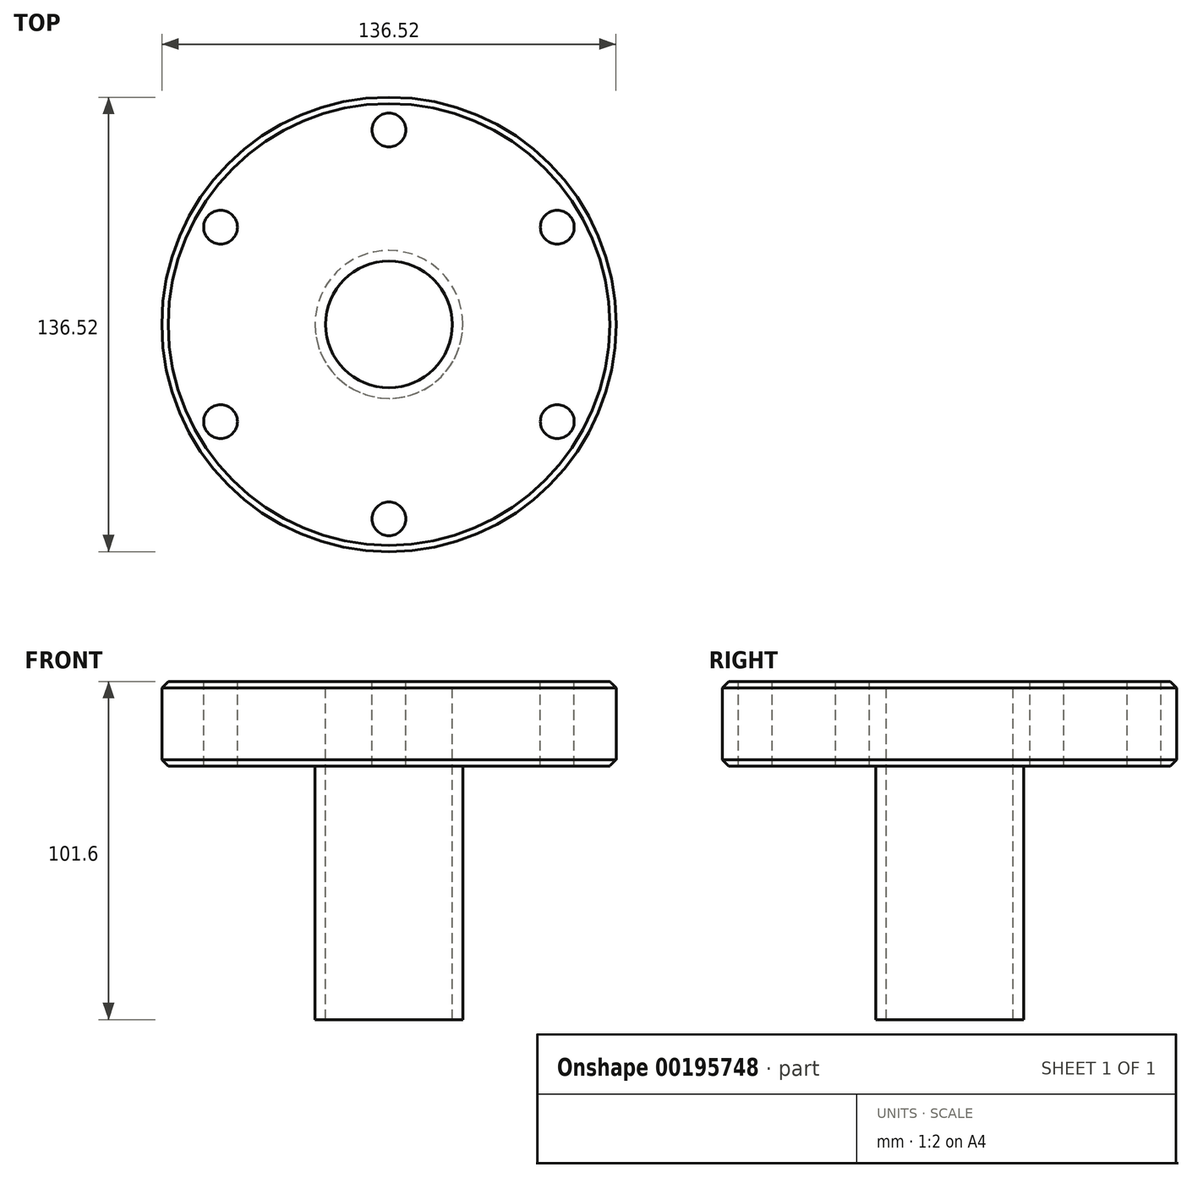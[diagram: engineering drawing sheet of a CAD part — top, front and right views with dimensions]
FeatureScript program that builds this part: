
annotation { "Feature Type Name" : "Feature", "Feature Type Description" : "" }
export const myFeature = defineFeature(function(context is Context, id is Id, definition is map)
    precondition{}
    {
        {
            var Q0;
            Q0=qCreatedBy(makeId("Top.planeOp"),FACE);
            var sketch = newSketch(context, id + "F0", { "sketchPlane" : qUnion([Q0])});
            skCircle(sketch, "E0", {"center": v(0, 0) * mm, "radius": 68.26 * mm});
            skSolve(sketch);
        }
        {
            var Q0;
            Q0=qSketchRegion(id+"F0",true);
            extrude(context, id + "F1", {"entities" : qUnion([Q0]), "depth" : 25.4 * mm});
        }
        {
            var Q0;
            Q0=makeQuery(id+"F1.opExtrude","CAP_FACE",FACE,{"disambiguationData":[OSD([sQuery(id+"F0.wireOp",EDGE,"E0")])],"isStart":true});
            var sketch = newSketch(context, id + "F2", { "sketchPlane" : qUnion([Q0])});
            skCircle(sketch, "E1", {"center": v(0, 0) * mm, "radius": 38.1 * mm});
            skSolve(sketch);
        }
        {
            var Q0;
            Q0=qSketchRegion(id+"F2",true);
            extrude(context, id + "F3", {"entities" : qUnion([Q0]), "operationType" : NewBodyOperationType.ADD, "depth" : 101.6 * mm});
        }
        {
            var Q0;
            Q0=makeQuery(id+"F1.opExtrude","CAP_FACE",FACE,{"disambiguationData":[OSD([sQuery(id+"F0.wireOp",EDGE,"E0")])],"isStart":false});
            var sketch = newSketch(context, id + "F4", { "sketchPlane" : qUnion([Q0])});
            skCircle(sketch, "E2", {"center": v(0, 0) * mm, "radius": 19.05 * mm});
            skSolve(sketch);
        }
        {
            var Q0;
            Q0=qSketchRegion(id+"F4",true);
            extrude(context, id + "F5", {"entities" : qUnion([Q0]), "operationType" : NewBodyOperationType.REMOVE, "oppositeDirection" : true, "depth" : 101.6 * mm});
        }
        {
            var Q0;
            Q0=makeQuery(id+"F5.boolean.opBoolean","COPY",FACE,{"derivedFrom":makeQuery(id+"F5.opExtrude","CAP_FACE",FACE,{"disambiguationData":[OSD([sQuery(id+"F4.wireOp",EDGE,"E2")])],"isStart":false})});
            var sketch = newSketch(context, id + "F6", { "sketchPlane" : qUnion([Q0])});
            skCircle(sketch, "E3", {"center": v(0, 0) * mm, "radius": 22.23 * mm});
            skSolve(sketch);
        }
        {
            var Q0;
            Q0=qSketchRegion(id+"F6",true);
            extrude(context, id + "F7", {"entities" : qUnion([Q0]), "operationType" : NewBodyOperationType.REMOVE, "oppositeDirection" : true, "depth" : 76.2 * mm});
        }
        {
            var Q0;
            Q0=makeQuery(id+"F1.opExtrude","CAP_FACE",FACE,{"disambiguationData":[OSD([sQuery(id+"F0.wireOp",EDGE,"E0")])],"isStart":false});
            var sketch = newSketch(context, id + "F8", { "sketchPlane" : qUnion([Q0])});
            skCircle(sketch, "E4", {"center": v(0, 58.42) * mm, "radius": 5.08 * mm});
            skCircle(sketch, "E5.1.0", {"center": v(-50.6, 29.21) * mm, "radius": 5.08 * mm});
            skCircle(sketch, "E5.2.0", {"center": v(-50.6, -29.2) * mm, "radius": 5.08 * mm});
            skCircle(sketch, "E5.3.0", {"center": v(0, -58.42) * mm, "radius": 5.08 * mm});
            skCircle(sketch, "E5.4.0", {"center": v(50.6, -29.21) * mm, "radius": 5.08 * mm});
            skCircle(sketch, "E5.5.0", {"center": v(50.6, 29.21) * mm, "radius": 5.08 * mm});
            skPoint(sketch, "E5.center", {"position": v(0, 0) * mm});
            skSolve(sketch);
        }
        {
            var Q0;
            Q0=qSketchRegion(id+"F8",true);
            extrude(context, id + "F9", {"entities" : qUnion([Q0]), "operationType" : NewBodyOperationType.REMOVE, "oppositeDirection" : true, "depth" : 25.4 * mm});
        }
        {
            var Q0;
            Q0=makeQuery(id+"F1.opExtrude","CAP_EDGE",EDGE,{"disambiguationData":[OSD([sQuery(id+"F0.wireOp",EDGE,"E0")])],"isStart":false});
            var Q1;
            Q1=makeQuery(id+"F1.opExtrude","CAP_EDGE",EDGE,{"disambiguationData":[OSD([sQuery(id+"F0.wireOp",EDGE,"E0")])],"isStart":true});
            chamfer(context, id + "F10", {"entities" : qUnion([Q0, Q1]), "width" : 1.9 * mm, "tangentPropagation" : true});
        }
        {
            var Q0;
            Q0=makeQuery(id+"F3.opExtrude","CAP_FACE",FACE,{"disambiguationData":[OSD([sQuery(id+"F2.wireOp",EDGE,"E1")])],"isStart":false});
            extrude(context, id + "F11", {"entities" : qUnion([Q0]), "operationType" : NewBodyOperationType.REMOVE, "oppositeDirection" : true, "depth" : 101.6 * mm});
        }
    });
